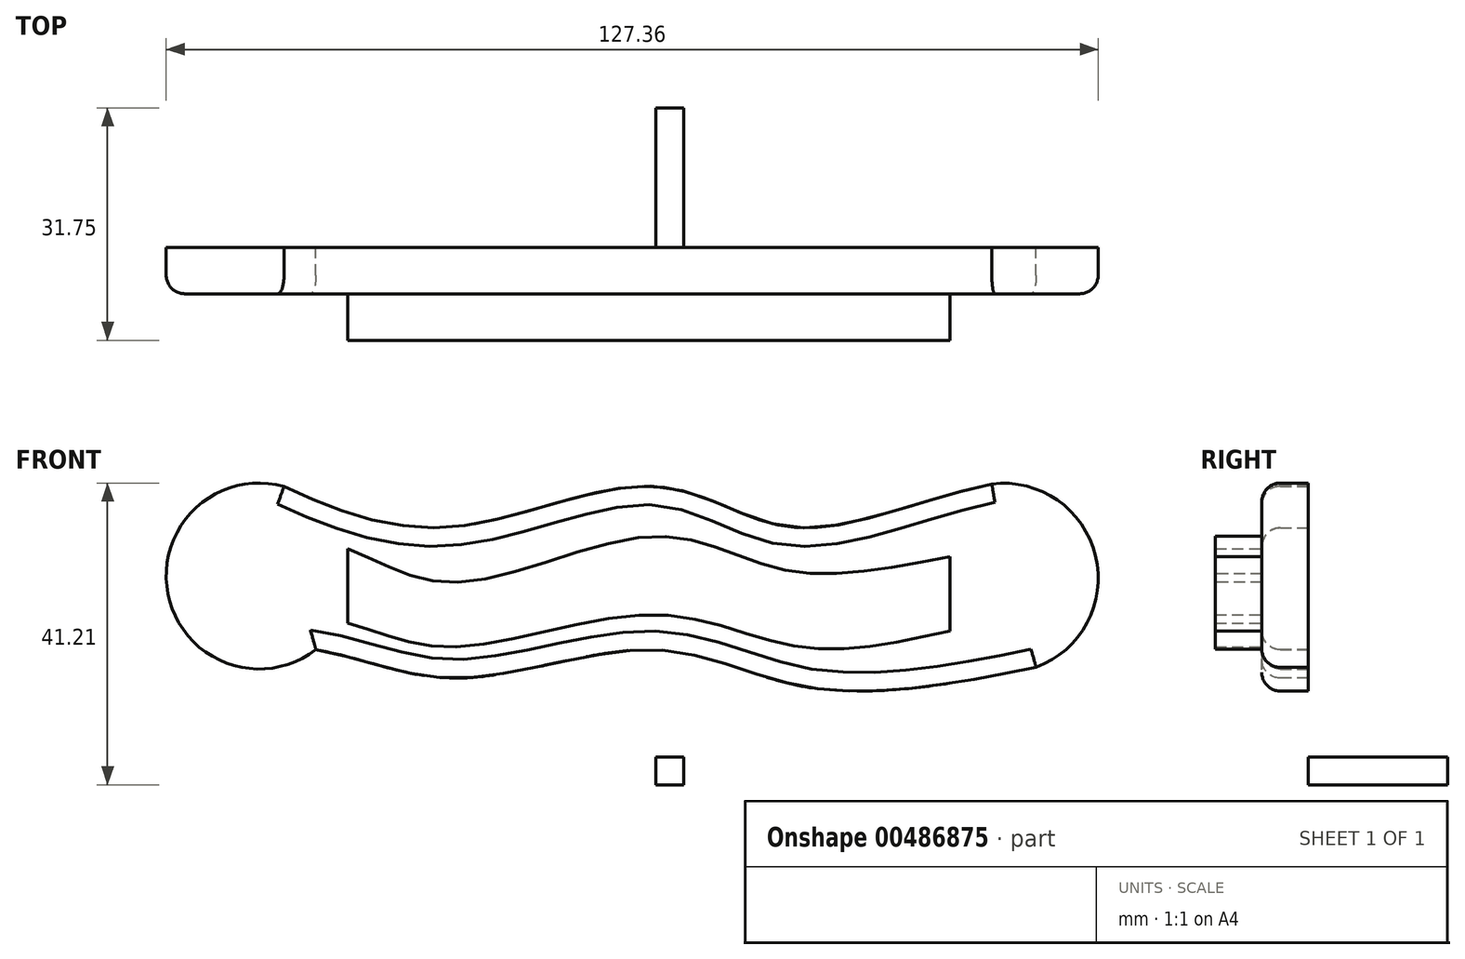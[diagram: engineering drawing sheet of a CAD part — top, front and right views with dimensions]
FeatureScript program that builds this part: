
annotation { "Feature Type Name" : "Feature", "Feature Type Description" : "" }
export const myFeature = defineFeature(function(context is Context, id is Id, definition is map)
    precondition{}
    {
        {
            var Q0;
            Q0=qCreatedBy(makeId("Front.planeOp"),FACE);
            var sketch = newSketch(context, id + "F0", { "sketchPlane" : qUnion([Q0])});
            skArc(sketch, "E0", {"start": v(-50.8, 40.74) * mm, "mid": v(-66.66, 26.08) * mm, "end": v(-46.45, 18.44) * mm});
            skArc(sketch, "E1", {"start": v(51.99, 16.04) * mm, "mid": v(60.1, 31.26) * mm, "end": v(45.92, 41.08) * mm});
            skFitSpline(sketch, "E2", {"points": [v(-50.8, 40.74) * mm, v(-27.84, 35.21) * mm, v(0, 40.74) * mm, v(18.07, 35.21) * mm, v(45.92, 41.08) * mm], "startDerivative": vector(86.64, -40.41) * mm, "endDerivative": vector(132.24, 29.83) * mm});
            skFitSpline(sketch, "E3", {"points": [v(-46.45, 18.44) * mm, v(-27.05, 14.56) * mm, v(0, 18.44) * mm, v(21.02, 13.27) * mm, v(51.99, 16.04) * mm], "startDerivative": vector(92.72, -15.8) * mm, "endDerivative": vector(110.17, 22.78) * mm});
            skLineSegment(sketch, "E4", {"start": v(-42.06, 32.23) * mm, "end": v(-42.06, 22.07) * mm});
            skLineSegment(sketch, "E5", {"start": v(40.19, 31.18) * mm, "end": v(40.19, 21.02) * mm});
            skFitSpline(sketch, "E6", {"points": [v(-42.06, 32.23) * mm, v(-27.1, 27.64) * mm, v(0, 33.92) * mm, v(17.7, 29.31) * mm, v(40.19, 31.18) * mm], "startDerivative": vector(65.05, -26.22) * mm, "endDerivative": vector(91.35, 18.2) * mm});
            skFitSpline(sketch, "E7", {"points": [v(-42.06, 22.07) * mm, v(-27.84, 18.8) * mm, v(0, 23.23) * mm, v(19.73, 18.8) * mm, v(40.19, 21.02) * mm], "startDerivative": vector(63.23, -16.78) * mm, "endDerivative": vector(84.32, 18.73) * mm});
            skSolve(sketch);
        }
        {
            var Q0;
            Q0=makeQuery(id+"F0.imprint","IMPRINT",FACE,{"disambiguationData":[TD([[makeQuery(id+"F0.imprint","IMPRINT",EDGE,{"derivedFrom":sQuery(id+"F0.wireOp",EDGE,"E0")}),1.0]])]});
            extrude(context, id + "F1", {"entities" : qUnion([Q0]), "depth" : 6.35 * mm});
        }
        {
            var Q0;
            Q0=makeQuery(id+"F0.imprint","IMPRINT",FACE,{"disambiguationData":[TD([[makeQuery(id+"F0.imprint","IMPRINT",EDGE,{"derivedFrom":sQuery(id+"F0.wireOp",EDGE,"E4")}),1.0]])]});
            extrude(context, id + "F2", {"entities" : qUnion([Q0]), "operationType" : NewBodyOperationType.ADD, "depth" : 12.7 * mm});
        }
        {
            var Q0;
            Q0=makeQuery(id+"F1.opExtrude","CAP_EDGE",EDGE,{"disambiguationData":[OSD([sQuery(id+"F0.wireOp",EDGE,"E0")])],"isStart":false});
            var Q1;
            Q1=makeQuery(id+"F1.opExtrude","CAP_EDGE",EDGE,{"disambiguationData":[OSD([sQuery(id+"F0.wireOp",EDGE,"E2")])],"isStart":false});
            var Q2;
            Q2=makeQuery(id+"F1.opExtrude","CAP_EDGE",EDGE,{"disambiguationData":[OSD([sQuery(id+"F0.wireOp",EDGE,"E3")])],"isStart":false});
            var Q3;
            Q3=makeQuery(id+"F1.opExtrude","CAP_EDGE",EDGE,{"disambiguationData":[OSD([sQuery(id+"F0.wireOp",EDGE,"E1")])],"isStart":false});
            fillet(context, id + "F3", {"entities" : qUnion([Q0, Q1, Q2, Q3]), "radius" : 2.54 * mm, "tangentPropagation" : true, "allowEdgeOverflow" : false});
        }
        {
            var Q0;
            Q0=qCreatedBy(makeId("Top.planeOp"),FACE);
            var sketch = newSketch(context, id + "F4", { "sketchPlane" : qUnion([Q0])});
            skLineSegment(sketch, "E8", {"start": v(0, 0) * mm, "end": v(0, 19.05) * mm});
            skLineSegment(sketch, "E9", {"start": v(3.81, 19.05) * mm, "end": v(0, 19.05) * mm});
            skLineSegment(sketch, "E10", {"start": v(3.81, 19.05) * mm, "end": v(3.81, 0) * mm});
            skLineSegment(sketch, "E11", {"start": v(3.81, 0) * mm, "end": v(0, 0) * mm});
            skSolve(sketch);
        }
        {
            var Q0;
            Q0=qSketchRegion(id+"F4",true);
            extrude(context, id + "F5", {"entities" : qUnion([Q0]), "depth" : 3.8 * mm});
        }
    });
